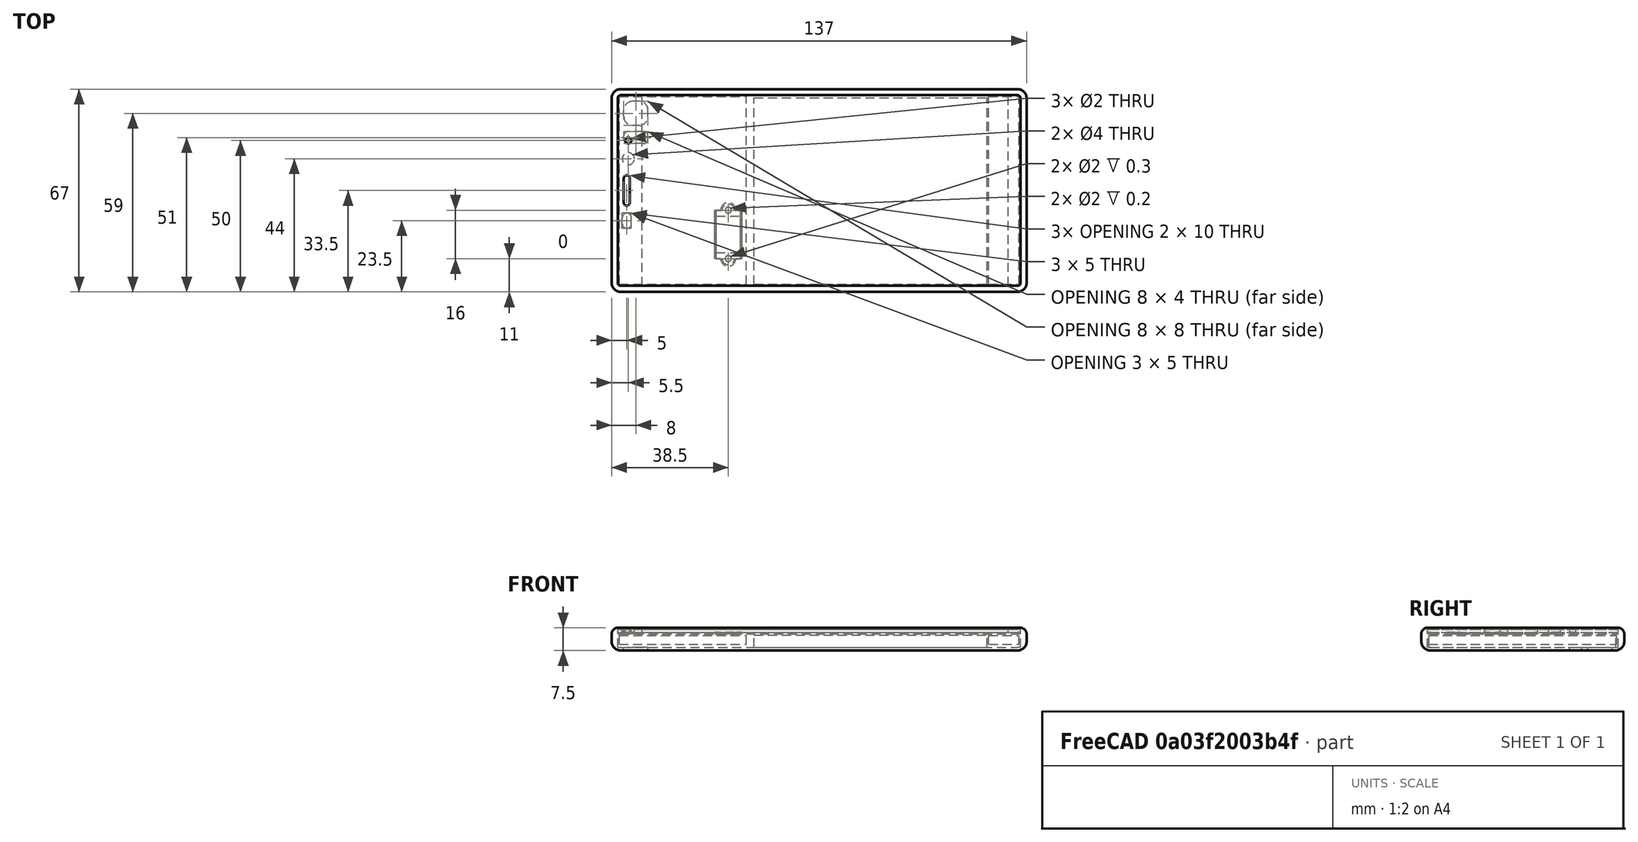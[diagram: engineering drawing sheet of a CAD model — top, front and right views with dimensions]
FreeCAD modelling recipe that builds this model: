
FCSTD DOCUMENT  (FreeCAD 0.16R6706 (Git))
Label: uCromy 2017
License: All rights reserved
LicenseURL: http://en.wikipedia.org/wiki/All_rights_reserved
objects: Part::Cut×26, Part::Box×22, Part::Fillet×13, Part::Cylinder×13, Part::MultiFuse×4
note: 78 computed .brp shape members not serialized (recipe doc carries the construction recipe); baked Part::Feature solids carry a one-line shape summary decoded from their .brp

FEATURE [Part::Box] Box  label="Cubo"
  Height = 7.5
  Length = 137
  Width = 67
FEATURE [Part::Fillet] Fillet
  Base = -> Box
  Edges = 8 edges r=3: [Edge1,Edge3,Edge4,Edge5,Edge7,Edge8,Edge9,Edge11]
FEATURE [Part::Fillet] Fillet001
  Base = -> Fillet
  Edges = 7 edges r=2: [Edge1,Edge5,Edge7,Edge8,Edge9,Edge10,Edge11]
FEATURE [Part::Box] Box001  label="Cubo001"
  Height = 10
  Length = 133
  Placement = pos=(2,2,5.5) rot=(0,0,1;0rad)
  Width = 63
FEATURE [Part::Fillet] Fillet002
  Base = -> Box001
  Edges = 4 edges r=1: [Edge1,Edge3,Edge5,Edge7]
  Placement = pos=(0,0,-4.5) rot=(0,0,1;0rad)
FEATURE [Part::Cut] Cut  label="Chassis"
  Base = -> Fillet001
  Tool = -> Fillet002
FEATURE [Part::Box] Box003  label="Cubo003"
  Height = 0.5
  Length = 133
  Placement = pos=(2,2,5.5) rot=(0,0,1;0rad)
  Width = 63
FEATURE [Part::Fillet] Fillet004  label="Dont show001"
  Base = -> Box003
  Edges = 4 edges r=1: [Edge1,Edge3,Edge5,Edge7]
FEATURE [Part::Box] Box004  label="Cubo004"
  Height = 0.5
  Length = 133
  Placement = pos=(2,2,5.5) rot=(0,0,1;0rad)
  Width = 63
FEATURE [Part::Fillet] Fillet005  label="Touchscreen"
  Base = -> Box004
  Edges = 4 edges r=1: [Edge1,Edge3,Edge5,Edge7]
  Placement = pos=(0,0,1.5) rot=(0,0,1;0rad)
FEATURE [Part::Box] Box005  label="Screen"
  Height = 1
  Length = 121
  Placement = pos=(10,2,6) rot=(0,0,1;0rad)
  Width = 63
FEATURE [Part::Box] Box006  label="Screen001"
  Height = 1
  Length = 8
  Placement = pos=(2,2,6) rot=(0,0,1;0rad)
  Width = 63
FEATURE [Part::Box] Box007  label="Screen002"
  Height = 1
  Length = 4
  Placement = pos=(131,2,6) rot=(0,0,1;0rad)
  Width = 63
FEATURE [Part::Fillet] Fillet006  label="Bottom"
  Base = -> Box007
  Edges = 2 edges r=1: [Edge5,Edge7]
FEATURE [Part::Fillet] Fillet007  label="Top"
  Base = -> Box006
  Edges = 2 edges r=1: [Edge1,Edge3]
FEATURE [Part::Box] Box008  label="Cubo005"
  Height = 0.2
  Length = 8
  Placement = pos=(35,10.5,1) rot=(0,0,1;0rad)
  Width = 16
FEATURE [Part::Cylinder] Cylinder  label="Cilindro"
  Angle = 360
  Height = 0.2
  Placement = pos=(39,10.5,1) rot=(0,0,1;0rad)
  Radius = 2
FEATURE [Part::Cylinder] Cylinder001  label="Cilindro001"
  Angle = 360
  Height = 0.2
  Placement = pos=(39,26.5,1) rot=(0,0,1;0rad)
  Radius = 2
FEATURE [Part::MultiFuse] Fusion  label="Chapa flex pantalla"
  Placement = pos=(-0.5,0.5,4.8) rot=(0,0,1;0rad)
  Shapes = -> [Box008,Cylinder001,Cylinder]
FEATURE [Part::Box] Box009  label="Cubo006"
  Height = 0.3
  Length = 9
  Placement = pos=(34,11,1) rot=(0,0,1;0rad)
  Width = 16
FEATURE [Part::Cylinder] Cylinder002  label="Cilindro002"
  Angle = 360
  Height = 0.3
  Placement = pos=(38.5,11,1) rot=(0,0,1;0rad)
  Radius = 2.5
FEATURE [Part::Cylinder] Cylinder003  label="Cilindro003"
  Angle = 360
  Height = 0.3
  Placement = pos=(38.5,27,1) rot=(0,0,1;0rad)
  Radius = 2.5
FEATURE [Part::MultiFuse] Fusion001  label="Agujero flex pantalla"
  Placement = pos=(0,0,4.4) rot=(0,0,1;0rad)
  Shapes = -> [Box009,Cylinder003,Cylinder002]
FEATURE [Part::Box] Box010  label="Cubo007"
  Height = 1.2
  Length = 8
  Placement = pos=(34.5,11,5) rot=(0,0,1;0rad)
  Width = 16
FEATURE [Part::Cylinder] Cylinder004  label="Cilindro004"
  Angle = 360
  Height = 10
  Placement = pos=(38.5,27,1) rot=(0,0,1;0rad)
  Radius = 1
FEATURE [Part::Cylinder] Cylinder005  label="Cilindro005"
  Angle = 360
  Height = 10
  Placement = pos=(38.5,11,1) rot=(0,0,1;0rad)
  Radius = 1
FEATURE [Part::Cut] Cut001
  Base = -> Box010
  Tool = -> Cylinder004
FEATURE [Part::Cut] Cut002
  Base = -> Cut001
  Tool = -> Cylinder005
FEATURE [Part::Cut] Cut003
  Base = -> Fusion001
  Tool = -> Cylinder005
FEATURE [Part::Cut] Cut004
  Base = -> Cut003
  Placement = pos=(0,0,0.4) rot=(0,0,1;0rad)
  Tool = -> Cylinder004
FEATURE [Part::Cut] Cut005
  Base = -> Fusion
  Tool = -> Cylinder004
FEATURE [Part::Cut] Cut006  label="Chapa flex"
  Base = -> Cut005
  Tool = -> Cylinder005
FEATURE [Part::Cylinder] Cylinder006  label="Cilindro006"
  Angle = 360
  Height = 10
  Placement = pos=(38.5,11,1) rot=(0,0,1;0rad)
  Radius = 1.5
FEATURE [Part::Cylinder] Cylinder007  label="Cilindro007"
  Angle = 360
  Height = 10
  Placement = pos=(38.5,27,1) rot=(0,0,1;0rad)
  Radius = 1.5
FEATURE [Part::Cut] Cut007
  Base = -> Cut002
  Tool = -> Cylinder007
FEATURE [Part::Cut] Cut008
  Base = -> Cut007
  Tool = -> Cylinder006
FEATURE [Part::MultiFuse] Fusion002  label="Dont show"
  Shapes = -> [Cut004,Cut008]
FEATURE [Part::Cut] Cut009
  Base = -> Fillet004
  Tool = -> Fusion002
FEATURE [Part::Box] Box011  label="Cubo008"
  Height = 0.3
  Length = 9
  Placement = pos=(34,11,5.5) rot=(0,0,1;0rad)
  Width = 2
FEATURE [Part::Box] Box012  label="Cubo009"
  Height = 0.3
  Length = 9
  Placement = pos=(34,25,5.5) rot=(0,0,1;0rad)
  Width = 2
FEATURE [Part::MultiFuse] Fusion003
  Shapes = -> [Cut009,Box011,Box012]
FEATURE [Part::Cylinder] Cylinder008  label="Cilindro008"
  Angle = 360
  Height = 0.1
  Placement = pos=(38.5,11,1) rot=(0,0,1;0rad)
  Radius = 1.2
FEATURE [Part::Cylinder] Cylinder009  label="Cilindro009"
  Angle = 360
  Height = 0.1
  Placement = pos=(38.5,27,1) rot=(0,0,1;0rad)
  Radius = 1.2
FEATURE [Part::Cut] Cut010
  Base = -> Fusion003
  Tool = -> Cylinder008
FEATURE [Part::Cut] Cut011
  Base = -> Cut010
  Tool = -> Cylinder009
FEATURE [Part::Cut] Cut012
  Base = -> Cut011
  Tool = -> Cylinder004
FEATURE [Part::Cut] Cut013
  Base = -> Cut012
  Tool = -> Cylinder005
FEATURE [Part::Box] Box013  label="PCB"
  Height = 3
  Length = 42
  Placement = pos=(2.5,2.5,2) rot=(0,0,1;0rad)
  Width = 62
FEATURE [Part::Box] Box014  label="Loud_Speaker"
  Height = 3
  Length = 10
  Placement = pos=(124.5,2.5,2) rot=(0,0,1;0rad)
  Width = 62
FEATURE [Part::Box] Box015  label="Battery"
  Height = 4.05
  Length = 77
  Placement = pos=(47,2.5,1.1) rot=(0,0,1;0rad)
  Width = 61.7
FEATURE [Part::Box] Box016  label="Cubo010"
  Height = 10
  Length = 2
  Placement = pos=(4,28.5,0) rot=(0,0,1;0rad)
  Width = 10
FEATURE [Part::Fillet] Fillet008
  Base = -> Box016
  Edges = 4 edges r=0.95: [Edge1,Edge3,Edge5,Edge7]
FEATURE [Part::Cut] Cut014
  Base = -> Fillet005
  Tool = -> Fillet008
FEATURE [Part::Cut] Cut015
  Base = -> Fillet007
  Tool = -> Fillet008
FEATURE [Part::Cylinder] Cylinder010  label="Cilindro010"
  Angle = 360
  Height = 10
  Placement = pos=(5.5,50,0) rot=(0,0,1;0rad)
  Radius = 1
FEATURE [Part::Cut] Cut016
  Base = -> Cut014
  Tool = -> Cylinder010
FEATURE [Part::Cut] Cut017
  Base = -> Cut013
  Tool = -> Cylinder010
FEATURE [Part::Cylinder] Cylinder011  label="Cilindro011"
  Angle = 360
  Height = 10
  Placement = pos=(5.5,44,0) rot=(0,0,1;0rad)
  Radius = 2
FEATURE [Part::Box] Box017  label="Cubo011"
  Height = 10
  Length = 3
  Placement = pos=(3.5,21,0) rot=(0,0,1;0rad)
  Width = 5
FEATURE [Part::Cylinder] Cylinder012  label="Cilindro012"
  Angle = 360
  Height = 2
  Placement = pos=(5.5,50,5.5) rot=(0,0,1;0rad)
  Radius = 1
FEATURE [Part::Cut] Cut018
  Base = -> Cut015
  Tool = -> Cylinder010
FEATURE [Part::Cut] Cut019
  Base = -> Cut017
  Tool = -> Cylinder011
FEATURE [Part::Cut] Cut020
  Base = -> Cut019
  Tool = -> Box017
FEATURE [Part::Box] Box018  label="Cubo012"
  Height = 10
  Length = 3
  Placement = pos=(3.5,21,0) rot=(0,0,1;0rad)
  Width = 5
FEATURE [Part::Fillet] Fillet009
  Base = -> Box018
  Edges = 4 edges r=1.49: [Edge1,Edge3,Edge5,Edge7]
FEATURE [Part::Cut] Cut021
  Base = -> Cut018
  Tool = -> Fillet009
FEATURE [Part::Cut] Cut022
  Base = -> Cut020
  Tool = -> Fillet008
FEATURE [Part::Cut] Cut023
  Base = -> Cut021
  Tool = -> Cylinder011
FEATURE [Part::Box] Box019  label="Cubo013"
  Height = 10
  Length = 8
  Placement = pos=(4,55,-1) rot=(0,0,1;0rad)
  Width = 8
FEATURE [Part::Fillet] Fillet010
  Base = -> Box019
  Edges = 4 edges r=3: [Edge1,Edge3,Edge5,Edge7]
FEATURE [Part::Box] Box020  label="Cubo014"
  Height = 1
  Length = 8
  Placement = pos=(4,55,-1) rot=(0,0,1;0rad)
  Width = 8
FEATURE [Part::Fillet] Fillet011
  Base = -> Box020
  Edges = 4 edges r=3: [Edge1,Edge3,Edge5,Edge7]
  Placement = pos=(0,0,1) rot=(0,0,1;0rad)
FEATURE [Part::Box] Box021  label="Cubo015"
  Height = 10
  Length = 8
  Placement = pos=(4,55,-1) rot=(0,0,1;0rad)
  Width = 4
FEATURE [Part::Fillet] Fillet012
  Base = -> Box021
  Edges = 4 edges r=1.5: [Edge1,Edge3,Edge5,Edge7]
  Placement = pos=(0,-6,0) rot=(0,0,1;0rad)
FEATURE [Part::Cut] Cut024
  Base = -> Cut
  Tool = -> Fillet010
FEATURE [Part::Box] Box022  label="Cubo016"
  Height = 1
  Length = 8
  Placement = pos=(4,55,-1) rot=(0,0,1;0rad)
  Width = 4
FEATURE [Part::Fillet] Fillet013
  Base = -> Box022
  Edges = 4 edges r=1.5: [Edge1,Edge3,Edge5,Edge7]
  Placement = pos=(0,-6,1) rot=(0,0,1;0rad)
FEATURE [Part::Cut] Cut025
  Base = -> Cut024
  Tool = -> Fillet012
